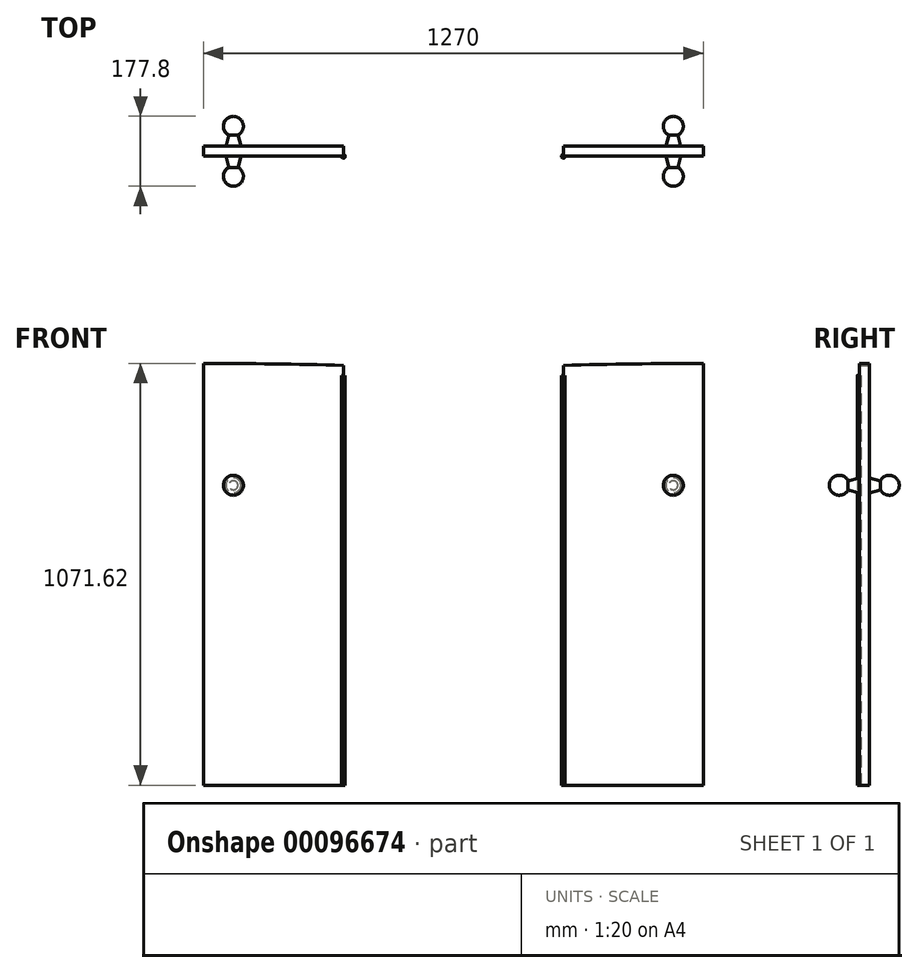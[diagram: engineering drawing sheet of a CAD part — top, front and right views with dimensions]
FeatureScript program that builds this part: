
annotation { "Feature Type Name" : "Feature", "Feature Type Description" : "" }
export const myFeature = defineFeature(function(context is Context, id is Id, definition is map)
    precondition{}
    {
        {
            var Q0;
            Q0=qCreatedBy(makeId("Front.planeOp"),FACE);
            var sketch = newSketch(context, id + "F0", { "sketchPlane" : qUnion([Q0])});
            skLineSegment(sketch, "E0.bottom", {"start": v(0, 0) * mm, "end": v(355.6, 0) * mm});
            skLineSegment(sketch, "E0.left", {"start": v(0, 0) * mm, "end": v(0, 1071.62) * mm});
            skLineSegment(sketch, "E0.right", {"start": v(355.6, 0) * mm, "end": v(355.6, 1066.8) * mm});
            skArc(sketch, "E1", {"start": v(355.6, 1066.8) * mm, "mid": v(177.82, 1070.41) * mm, "end": v(0, 1071.62) * mm});
            skLineSegment(sketch, "E2", {"start": v(917.31, 1054.16) * mm, "end": v(917.31, -67.69) * mm});
            skSolve(sketch);
        }
        {
            var Q0;
            Q0 = qSketchRegion(id + "F0", true);
            extrude(context, id + "F1", {"entities" : qUnion([Q0]), "endBound" : BoundingType.SYMMETRIC, "depth" : 25.4 * mm});
        }
        {
            var Q0;
            Q0=qCreatedBy(makeId("Top.planeOp"),FACE);
            cPlane(context, id + "F2", {"entities" : qUnion([Q0]), "cplaneType" : CPlaneType.OFFSET, "offset" : 762 * mm, "width" : 152.4 * mm, "height" : 152.4 * mm});
        }
        {
            var Q0;
            Q0=qCreatedBy(id+"F2.planeOp",FACE);
            var sketch = newSketch(context, id + "F3", { "sketchPlane" : qUnion([Q0])});
            skArc(sketch, "E3", {"start": v(64.7, -40.86) * mm, "mid": v(51.5, -69.42) * mm, "end": v(76.2, -88.9) * mm});
            skLineSegment(sketch, "E4", {"start": v(57.15, -12.7) * mm, "end": v(64.7, -40.86) * mm});
            skLineSegment(sketch, "E5", {"start": v(57.15, -12.7) * mm, "end": v(76.2, -12.7) * mm});
            skLineSegment(sketch, "E6", {"start": v(76.2, -12.7) * mm, "end": v(76.2, -88.9) * mm});
            skSolve(sketch);
        }
        {
            var Q0;
            Q0=makeQuery(id+"F1.opExtrude","CAP_FACE",FACE,{"disambiguationData":[OSD([sQuery(id+"F0.wireOp",EDGE,"E0.bottom"),sQuery(id+"F0.wireOp",EDGE,"E0.left"),sQuery(id+"F0.wireOp",EDGE,"E0.right"),sQuery(id+"F0.wireOp",EDGE,"E1")])],"isStart":false});
            var sketch = newSketch(context, id + "F4", { "sketchPlane" : qUnion([Q0])});
            skCircle(sketch, "E7", {"center": v(76.2, 762) * mm, "radius": 28.9 * mm});
            skSolve(sketch);
        }
        {
            var Q0;
            Q0=makeQuery(id+"F3.imprint","IMPRINT",FACE,{"disambiguationData":[TD([[makeQuery(id+"F3.imprint","IMPRINT",EDGE,{"derivedFrom":sQuery(id+"F3.wireOp",EDGE,"E3")}),1.0]])]});
            var Q1;
            Q1=sQuery(id+"F4.wireOp",EDGE,"E7");
            sweep(context, id + "F5", {"profiles" : qUnion([Q0]), "path" : qUnion([Q1])});
        }
        {
            var Q0;
            Q0=makeQuery(id+"F5.opSweep","SWEPT_BODY",BODY,{"disambiguationData":[OSD([sQuery(id+"F3.wireOp",EDGE,"E3"),sQuery(id+"F3.wireOp",EDGE,"E4"),sQuery(id+"F3.wireOp",EDGE,"E5"),sQuery(id+"F3.wireOp",EDGE,"E6"),sQuery(id+"F4.wireOp",EDGE,"E7")])]});
            var Q1;
            Q1=qCreatedBy(makeId("Front.planeOp"),FACE);
            mirror(context, id + "F6", {"operationType" : NewBodyOperationType.ADD, "entities" : qUnion([Q0]), "mirrorPlane" : qUnion([Q1])});
        }
        {
            var Q0;
            Q0=makeQuery(id+"F1.opExtrude","SWEPT_FACE",FACE,{"disambiguationData":[OSD([sQuery(id+"F0.wireOp",EDGE,"E0.bottom")])]});
            var sketch = newSketch(context, id + "F7", { "sketchPlane" : qUnion([Q0])});
            skCircle(sketch, "E8", {"center": v(355.6, 12.7) * mm, "radius": 4.76 * mm});
            skSolve(sketch);
        }
        {
            var Q0;
            Q0 = qSketchRegion(id + "F7", true);
            extrude(context, id + "F8", {"entities" : qUnion([Q0]), "operationType" : NewBodyOperationType.ADD, "oppositeDirection" : true, "depth" : 1041.4 * mm});
        }
        {
            var Q0;
            Q0=qCreatedBy(makeId("Right.planeOp"),FACE);
            cPlane(context, id + "F9", {"entities" : qUnion([Q0]), "cplaneType" : CPlaneType.OFFSET, "offset" : 635 * mm, "width" : 152.4 * mm, "height" : 152.4 * mm});
        }
        {
            var Q0;
            Q0=makeQuery(id+"F1.opExtrude","SWEPT_BODY",BODY,{"disambiguationData":[OSD([sQuery(id+"F0.wireOp",EDGE,"E0.bottom"),sQuery(id+"F0.wireOp",EDGE,"E0.left"),sQuery(id+"F0.wireOp",EDGE,"E0.right"),sQuery(id+"F0.wireOp",EDGE,"E1")])]});
            var Q1;
            Q1=qCreatedBy(id+"F9.planeOp",FACE);
            mirror(context, id + "F10", {"entities" : qUnion([Q0]), "mirrorPlane" : qUnion([Q1])});
        }
    });
